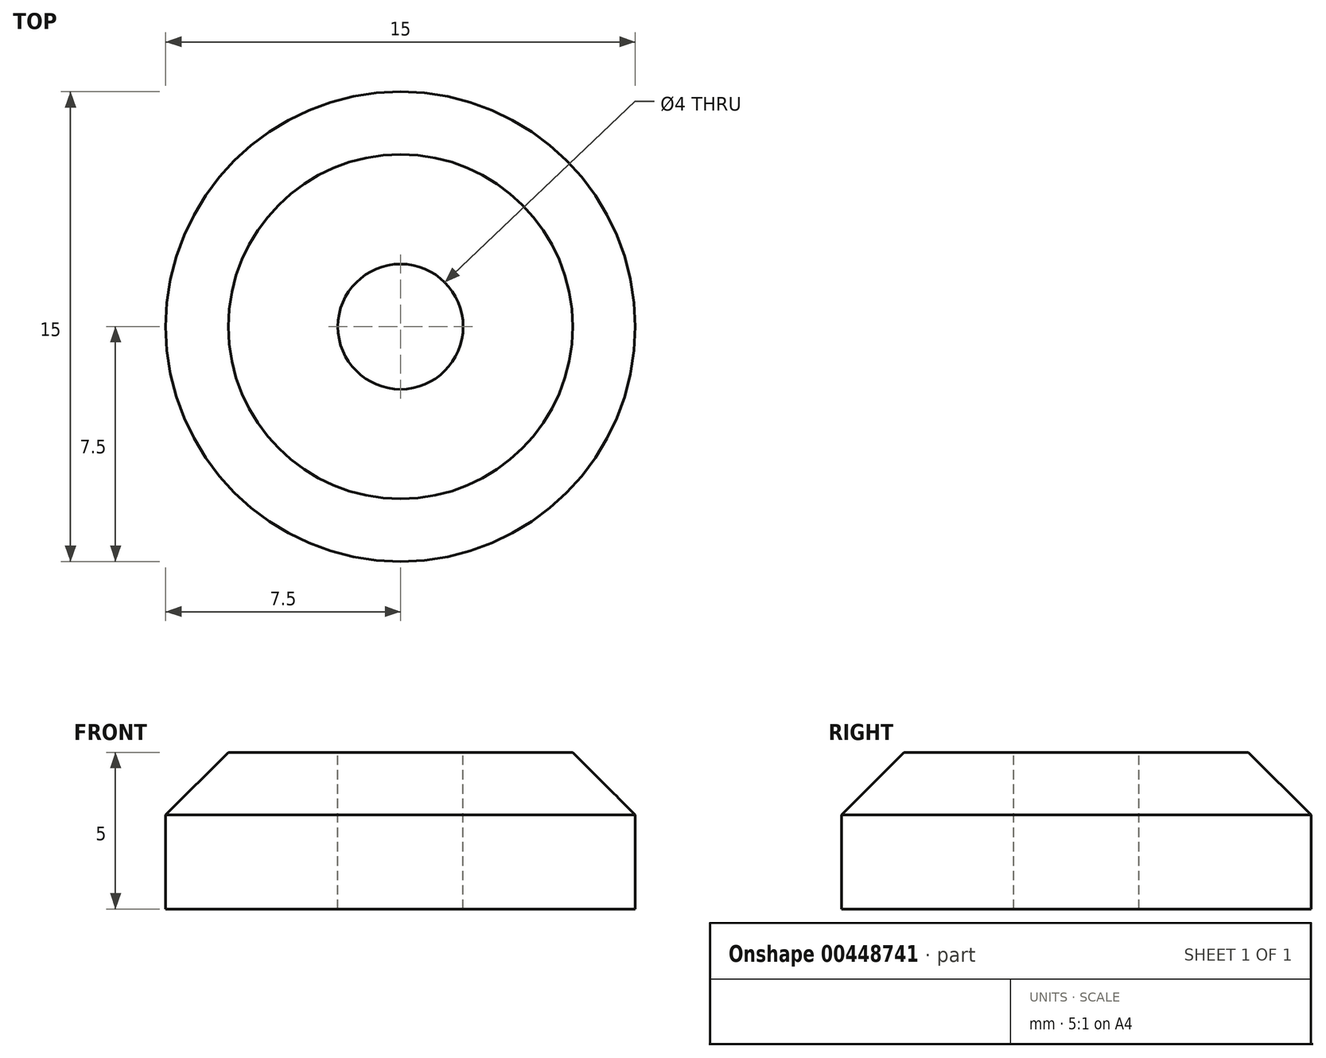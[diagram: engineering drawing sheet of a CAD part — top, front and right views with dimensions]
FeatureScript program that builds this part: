
annotation { "Feature Type Name" : "Feature", "Feature Type Description" : "" }
export const myFeature = defineFeature(function(context is Context, id is Id, definition is map)
    precondition{}
    {
        {
            var Q0;
            Q0=qCreatedBy(makeId("Top.planeOp"),FACE);
            var sketch = newSketch(context, id + "F0", { "sketchPlane" : qUnion([Q0])});
            skCircle(sketch, "E0", {"center": v(0, 0) * mm, "radius": 7.5 * mm});
            skSolve(sketch);
        }
        {
            var Q0;
            Q0 = qSketchRegion(id + "F0", true);
            extrude(context, id + "F1", {"entities" : qUnion([Q0]), "depth" : 5 * mm});
        }
        {
            var Q0;
            Q0=makeQuery(id+"F1.opExtrude","CAP_FACE",FACE,{"disambiguationData":[OSD([sQuery(id+"F0.wireOp",EDGE,"E0")])],"isStart":false});
            var sketch = newSketch(context, id + "F2", { "sketchPlane" : qUnion([Q0])});
            skCircle(sketch, "E1", {"center": v(0, 0) * mm, "radius": 2 * mm});
            skSolve(sketch);
        }
        {
            var Q0;
            Q0 = qSketchRegion(id + "F2", true);
            extrude(context, id + "F3", {"entities" : qUnion([Q0]), "operationType" : NewBodyOperationType.REMOVE, "oppositeDirection" : true, "depth" : 25 * mm});
        }
        {
            var Q0;
            Q0=makeQuery(id+"F1.opExtrude","CAP_EDGE",EDGE,{"disambiguationData":[OSD([sQuery(id+"F0.wireOp",EDGE,"E0")])],"isStart":false});
            chamfer(context, id + "F4", {"entities" : qUnion([Q0]), "width" : 2 * mm, "tangentPropagation" : true});
        }
    });
